# Revit family: Faucet-Valves_and_Controls-KOHLER-NATEO-K-882A
name_source: partatom
category: Plumbing Fixtures
revit_build: Autodesk Revit 2017 (Build: 20160225_1515(x64)
units: mm (PartAtom-declared; Revit-internal decimal feet)

## family parameters
Cut with Voids When Loaded = No
Host = Face
OmniClass Number = 23.27.31.00
OmniClass Title = Valves
Part Type = Normal
Room Calculation Point = No
Round Connector Dimension = Use Diameter
Shared = No

## types (6) — shared parameters
ADA Compliant = No
Assembly Code = D2020
CW Connection = Yes
Cold Water Inlet = Cold Water Inlet
Date Modified = 07/17/2020
Default Elevation = 47 1/4"
Description = Recessed Bath Shower Valve
Drain Included = No
Flow Rate = 0 GPM
HW Connection = Yes
Height = 6 5/16"
Hot Water Inlet = Hot Water Inlet
Length = 5 5/16"
Manufacturer = KOHLER Co.
Master Format 2014 = 22.11.00
Master Format 2014 Name = Residential Faucets, Supplies, and Trim
Material = Solid Brass Construction
Pressure = 0.00 psi
Product Name = NATEO
Tempered Water Outlet1 = Tempered Water Outlet1
Tempered Water Outlet2 = Tempered Water Outlet2
URL = https://kohler.com.au
Vent Connection = No
Waste Connection = No
Waste Water Outlet = Waste Water Outlet
WaterSense Certified = No
Width = 3 7/16"

## per-type parameters (varying)
| type | Finish | Model | Type |
| 2BL-Orignal Black | Kohler-Metal-2BL-Original_Black | K-882A-2BL | 2 |
| 2BZ-Oil-Rubbed Bronze | Kohler-Metal-2BZ-Oil_Rubbed_Bronze | K-882A-2BZ | 3 |
| CP-Polished Chrome | Kohler-Metal-CP-Polished_Chrome | K-882A-CP | 1 |
| RGD-Vibrant Rose Gold | Kohler-Metal-RGD-Polished_Rose_Gold | K-882A-RGD | 4 |
| TT-Vibrant Titanium | Kohler-Metal-TT-Vibrant_Titanium | K-882A-TT | 5 |
| BN-Vibrant Brushed Nickel | Kohler-Metal-BN-Vibrant_Brushed_Nickel | K-882A-BN | 6 |

## geometry (parser evidence)
native form markers: Sweep x4
no freeform markers — native parametric forms only
